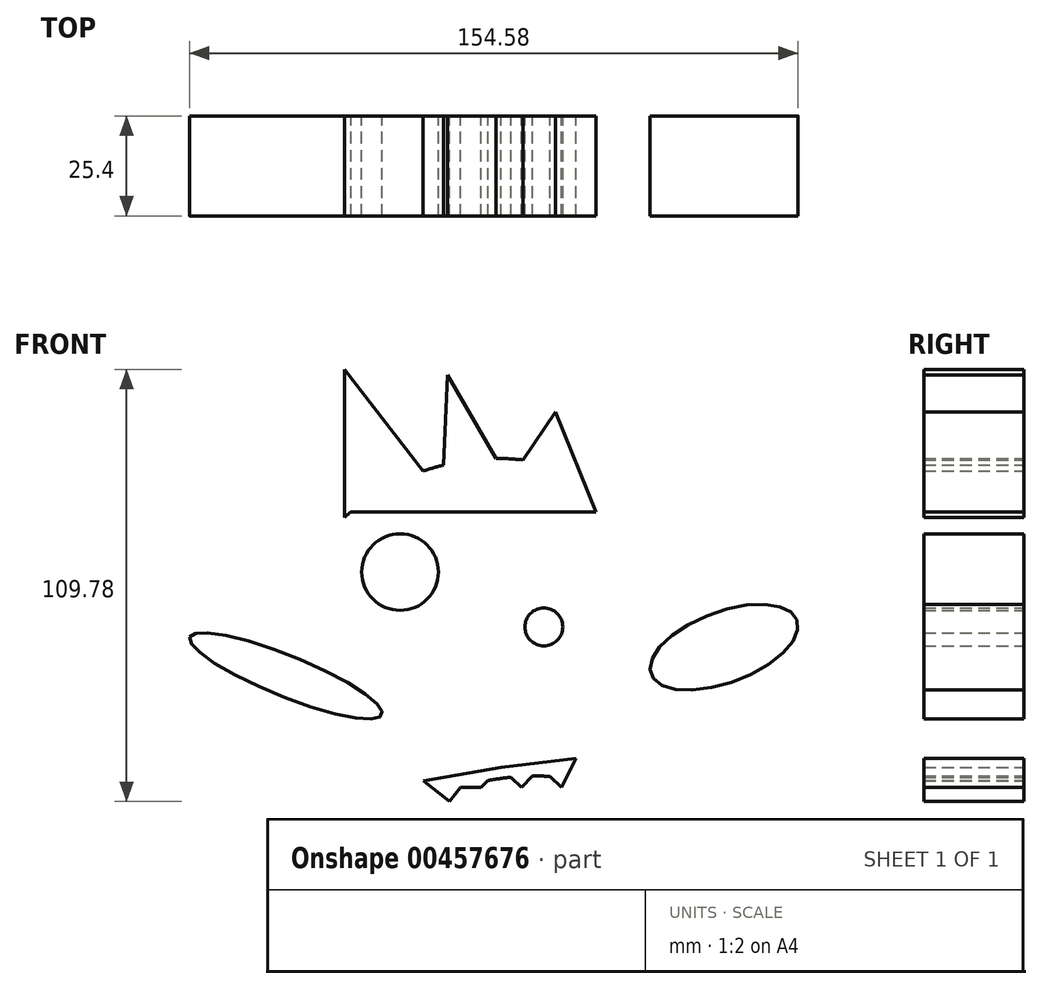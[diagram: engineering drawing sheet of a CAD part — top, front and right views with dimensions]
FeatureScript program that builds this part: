
annotation { "Feature Type Name" : "Feature", "Feature Type Description" : "" }
export const myFeature = defineFeature(function(context is Context, id is Id, definition is map)
    precondition{}
    {
        {
            var Q0;
            Q0=qCreatedBy(makeId("Front.planeOp"),FACE);
            var sketch = newSketch(context, id + "F0", { "sketchPlane" : qUnion([Q0])});
            skCircle(sketch, "E0", {"center": v(4.33, 0) * mm, "radius": 58.36 * mm});
            skCircle(sketch, "E1", {"center": v(-20.56, 29.51) * mm, "radius": 9.73 * mm});
            skCircle(sketch, "E2", {"center": v(17.31, 26.36) * mm, "radius": 10.85 * mm});
            skCircle(sketch, "E3", {"center": v(0, 0) * mm, "radius": 14.96 * mm});
            skArc(sketch, "E4", {"start": v(36.2, -26.36) * mm, "mid": v(6.21, -22.76) * mm, "end": v(-22.03, -33.44) * mm});
            skLineSegment(sketch, "E5", {"start": v(-22.03, -33.44) * mm, "end": v(36.2, -26.36) * mm});
            skLineSegment(sketch, "E6", {"start": v(-34.7, 43.39) * mm, "end": v(-34.7, 81) * mm});
            skLineSegment(sketch, "E7", {"start": v(-34.7, 81) * mm, "end": v(-9.93, 48.9) * mm});
            skLineSegment(sketch, "E8", {"start": v(-9.93, 48.9) * mm, "end": v(-8.51, 79.6) * mm});
            skLineSegment(sketch, "E9", {"start": v(-8.51, 79.6) * mm, "end": v(7.03, 52.73) * mm});
            skLineSegment(sketch, "E10", {"start": v(7.03, 52.73) * mm, "end": v(18.9, 70.15) * mm});
            skLineSegment(sketch, "E11", {"start": v(18.9, 70.15) * mm, "end": v(29.2, 44.82) * mm});
            skLineSegment(sketch, "E12", {"start": v(29.2, 44.82) * mm, "end": v(-33.05, 44.82) * mm});
            skEllipse(sketch, "E13", {"center": v(61.75, 10.44) * mm, "majorRadius": 19.75 * mm, "minorRadius": 9.04 * mm, "majorAxis": v(0.94, 0.35)});
            skEllipse(sketch, "E14", {"center": v(-49.58, 3.15) * mm, "majorRadius": 26.3 * mm, "minorRadius": 5.21 * mm, "majorAxis": v(-0.93, 0.37)});
            skLineSegment(sketch, "E15", {"start": v(-14.6, -23.54) * mm, "end": v(-8.05, -28.78) * mm});
            skLineSegment(sketch, "E16", {"start": v(-8.05, -28.78) * mm, "end": v(-5.23, -25.24) * mm});
            skLineSegment(sketch, "E17", {"start": v(-5.23, -25.24) * mm, "end": v(0, -25.24) * mm});
            skLineSegment(sketch, "E18", {"start": v(0, -25.24) * mm, "end": v(5.05, -20.13) * mm});
            skLineSegment(sketch, "E19", {"start": v(5.05, -20.13) * mm, "end": v(10.23, -25.24) * mm});
            skLineSegment(sketch, "E20", {"start": v(10.23, -25.24) * mm, "end": v(15.27, -20.13) * mm});
            skLineSegment(sketch, "E21", {"start": v(15.27, -20.13) * mm, "end": v(20.45, -25.24) * mm});
            skLineSegment(sketch, "E22", {"start": v(20.45, -25.24) * mm, "end": v(24.17, -17.77) * mm});
            skLineSegment(sketch, "E23", {"start": v(24.17, -17.77) * mm, "end": v(5.05, -20.13) * mm});
            skLineSegment(sketch, "E24", {"start": v(5.05, -20.13) * mm, "end": v(-14.6, -23.54) * mm});
            skCircle(sketch, "E25", {"center": v(15.96, 15.6) * mm, "radius": 4.8 * mm});
            skCircle(sketch, "E26", {"center": v(-20.56, 26.24) * mm, "radius": 3.46 * mm});
            skSolve(sketch);
        }
        {
            var Q0;
            {var subQ0=sQuery(id+"F0.wireOp",EDGE,"E13");var subQ1=sQuery(id+"F0.wireOp",EDGE,"E0");var subQ2=makeQuery(id+"F0.imprint","INTERSECT",VERTEX,{"disambiguationData":[OD(0.0)],"derivedFrom":[subQ1,subQ0]});Q0=makeQuery(id+"F0.imprint","IMPRINT",FACE,{"disambiguationData":[TD([[makeQuery(id+"F0.imprint","IMPRINT",EDGE,{"disambiguationData":[TD([[subQ2,1.0]])],"derivedFrom":subQ1}),-1.0]])]});}
            var Q1;
            {var subQ0=sQuery(id+"F0.wireOp",EDGE,"E11");var subQ1=sQuery(id+"F0.wireOp",EDGE,"E0");var subQ2=makeQuery(id+"F0.imprint","INTERSECT",VERTEX,{"derivedFrom":[subQ1,subQ0]});Q1=makeQuery(id+"F0.imprint","IMPRINT",FACE,{"disambiguationData":[TD([[makeQuery(id+"F0.imprint","IMPRINT",EDGE,{"disambiguationData":[TD([[subQ2,-1.0]])],"derivedFrom":subQ1}),-1.0]])]});}
            var Q2;
            {var subQ0=sQuery(id+"F0.wireOp",EDGE,"E10");var subQ1=sQuery(id+"F0.wireOp",EDGE,"E0");var subQ2=makeQuery(id+"F0.imprint","INTERSECT",VERTEX,{"derivedFrom":[subQ1,subQ0]});Q2=makeQuery(id+"F0.imprint","IMPRINT",FACE,{"disambiguationData":[TD([[makeQuery(id+"F0.imprint","IMPRINT",EDGE,{"disambiguationData":[TD([[subQ2,-1.0]])],"derivedFrom":subQ1}),1.0]])]});}
            var Q3;
            {var subQ0=sQuery(id+"F0.wireOp",EDGE,"E9");var subQ1=sQuery(id+"F0.wireOp",EDGE,"E0");var subQ2=makeQuery(id+"F0.imprint","INTERSECT",VERTEX,{"derivedFrom":[subQ1,subQ0]});Q3=makeQuery(id+"F0.imprint","IMPRINT",FACE,{"disambiguationData":[TD([[makeQuery(id+"F0.imprint","IMPRINT",EDGE,{"disambiguationData":[TD([[subQ2,-1.0]])],"derivedFrom":subQ1}),-1.0]])]});}
            var Q4;
            {var subQ0=sQuery(id+"F0.wireOp",EDGE,"E8");var subQ1=sQuery(id+"F0.wireOp",EDGE,"E0");var subQ2=makeQuery(id+"F0.imprint","INTERSECT",VERTEX,{"derivedFrom":[subQ1,subQ0]});Q4=makeQuery(id+"F0.imprint","IMPRINT",FACE,{"disambiguationData":[TD([[makeQuery(id+"F0.imprint","IMPRINT",EDGE,{"disambiguationData":[TD([[subQ2,-1.0]])],"derivedFrom":subQ1}),1.0]])]});}
            var Q5;
            {var subQ0=sQuery(id+"F0.wireOp",EDGE,"E14");var subQ1=sQuery(id+"F0.wireOp",EDGE,"E0");var subQ2=makeQuery(id+"F0.imprint","INTERSECT",VERTEX,{"disambiguationData":[OD(0.0)],"derivedFrom":[subQ1,subQ0]});Q5=makeQuery(id+"F0.imprint","IMPRINT",FACE,{"disambiguationData":[TD([[makeQuery(id+"F0.imprint","IMPRINT",EDGE,{"disambiguationData":[TD([[subQ2,-1.0]])],"derivedFrom":subQ1}),-1.0]])]});}
            var Q6;
            {var subQ0=sQuery(id+"F0.wireOp",EDGE,"E13");var subQ1=sQuery(id+"F0.wireOp",EDGE,"E0");var subQ2=makeQuery(id+"F0.imprint","INTERSECT",VERTEX,{"disambiguationData":[OD(0.0)],"derivedFrom":[subQ1,subQ0]});Q6=makeQuery(id+"F0.imprint","IMPRINT",FACE,{"disambiguationData":[TD([[makeQuery(id+"F0.imprint","IMPRINT",EDGE,{"disambiguationData":[TD([[subQ2,1.0]])],"derivedFrom":subQ1}),1.0]])]});}
            var Q7;
            {var subQ4=sQuery(id+"F0.wireOp",EDGE,"E6");Q7=makeQuery(id+"F0.imprint","IMPRINT",FACE,{"disambiguationData":[TD([[makeQuery(id+"F0.imprint","IMPRINT",EDGE,{"derivedFrom":subQ4}),-1.0]])]});}
            var Q8;
            {var subQ0=sQuery(id+"F0.wireOp",EDGE,"E14");var subQ1=sQuery(id+"F0.wireOp",EDGE,"E0");var subQ2=makeQuery(id+"F0.imprint","INTERSECT",VERTEX,{"disambiguationData":[OD(0.0)],"derivedFrom":[subQ1,subQ0]});Q8=makeQuery(id+"F0.imprint","IMPRINT",FACE,{"disambiguationData":[TD([[makeQuery(id+"F0.imprint","IMPRINT",EDGE,{"disambiguationData":[TD([[subQ2,-1.0]])],"derivedFrom":subQ1}),1.0]])]});}
            var Q9;
            {var subQ0=sQuery(id+"F0.wireOp",EDGE,"E12");Q9=makeQuery(id+"F0.imprint","IMPRINT",FACE,{"disambiguationData":[TD([[makeQuery(id+"F0.imprint","IMPRINT",EDGE,{"derivedFrom":subQ0}),-1.0]])]});}
            var Q10;
            {var subQ0=sQuery(id+"F0.wireOp",EDGE,"E20");var subQ1=sQuery(id+"F0.wireOp",EDGE,"E4");var subQ2=makeQuery(id+"F0.imprint","INTERSECT",VERTEX,{"derivedFrom":[subQ1,subQ0]});Q10=makeQuery(id+"F0.imprint","IMPRINT",FACE,{"disambiguationData":[TD([[makeQuery(id+"F0.imprint","IMPRINT",EDGE,{"disambiguationData":[TD([[subQ2,-1.0]])],"derivedFrom":subQ1}),1.0]])]});}
            var Q11;
            {var subQ0=sQuery(id+"F0.wireOp",EDGE,"E22");var subQ1=sQuery(id+"F0.wireOp",EDGE,"E4");var subQ2=makeQuery(id+"F0.imprint","INTERSECT",VERTEX,{"derivedFrom":[subQ1,subQ0]});Q11=makeQuery(id+"F0.imprint","IMPRINT",FACE,{"disambiguationData":[TD([[makeQuery(id+"F0.imprint","IMPRINT",EDGE,{"disambiguationData":[TD([[subQ2,-1.0]])],"derivedFrom":subQ1}),1.0]])]});}
            var Q12;
            {var subQ10=sQuery(id+"F0.wireOp",EDGE,"E23");Q12=makeQuery(id+"F0.imprint","IMPRINT",FACE,{"disambiguationData":[TD([[makeQuery(id+"F0.imprint","IMPRINT",EDGE,{"derivedFrom":subQ10}),1.0]])]});}
            var Q13;
            {var subQ0=sQuery(id+"F0.wireOp",EDGE,"E16");Q13=makeQuery(id+"F0.imprint","IMPRINT",FACE,{"disambiguationData":[TD([[makeQuery(id+"F0.imprint","IMPRINT",EDGE,{"derivedFrom":subQ0}),1.0]])]});}
            var Q14;
            {var subQ4=sQuery(id+"F0.wireOp",EDGE,"E24");Q14=makeQuery(id+"F0.imprint","IMPRINT",FACE,{"disambiguationData":[TD([[makeQuery(id+"F0.imprint","IMPRINT",EDGE,{"derivedFrom":subQ4}),1.0]])]});}
            var Q15;
            {var subQ0=sQuery(id+"F0.wireOp",EDGE,"E19");var subQ1=sQuery(id+"F0.wireOp",EDGE,"E4");var subQ2=makeQuery(id+"F0.imprint","INTERSECT",VERTEX,{"derivedFrom":[subQ1,subQ0]});Q15=makeQuery(id+"F0.imprint","IMPRINT",FACE,{"disambiguationData":[TD([[makeQuery(id+"F0.imprint","IMPRINT",EDGE,{"disambiguationData":[TD([[subQ2,-1.0]])],"derivedFrom":subQ1}),-1.0]])]});}
            var Q16;
            {var subQ0=sQuery(id+"F0.wireOp",EDGE,"E17");Q16=makeQuery(id+"F0.imprint","IMPRINT",FACE,{"disambiguationData":[TD([[makeQuery(id+"F0.imprint","IMPRINT",EDGE,{"derivedFrom":subQ0}),1.0]])]});}
            var Q17;
            {var subQ0=sQuery(id+"F0.wireOp",EDGE,"E21");var subQ1=sQuery(id+"F0.wireOp",EDGE,"E4");var subQ2=makeQuery(id+"F0.imprint","INTERSECT",VERTEX,{"derivedFrom":[subQ1,subQ0]});Q17=makeQuery(id+"F0.imprint","IMPRINT",FACE,{"disambiguationData":[TD([[makeQuery(id+"F0.imprint","IMPRINT",EDGE,{"disambiguationData":[TD([[subQ2,-1.0]])],"derivedFrom":subQ1}),-1.0]])]});}
            var Q18;
            {var subQ0=sQuery(id+"F0.wireOp",EDGE,"Bl3zAe94-TYqv-aWNH-iYuO-jx3CQXA83sbJ");var subQ1=sQuery(id+"F0.wireOp",EDGE,"E1");var subQ2=makeQuery(id+"F0.imprint","INTERSECT",VERTEX,{"disambiguationData":[OD(0.0)],"derivedFrom":[subQ1,subQ0]});Q18=makeQuery(id+"F0.imprint","IMPRINT",FACE,{"disambiguationData":[TD([[makeQuery(id+"F0.imprint","IMPRINT",EDGE,{"disambiguationData":[TD([[subQ2,-1.0]])],"derivedFrom":subQ1}),1.0]])]});}
            var Q19;
            Q19=makeQuery(id+"F0.imprint","IMPRINT",FACE,{"disambiguationData":[TD([[makeQuery(id+"F0.imprint","IMPRINT",EDGE,{"derivedFrom":sQuery(id+"F0.wireOp",EDGE,"E3")}),-1.0]])]});
            var Q20;
            {var subQ0=sQuery(id+"F0.wireOp",EDGE,"Bl3zAe94-TYqv-aWNH-iYuO-jx3CQXA83sbJ");var subQ1=sQuery(id+"F0.wireOp",EDGE,"E1");var subQ2=makeQuery(id+"F0.imprint","INTERSECT",VERTEX,{"disambiguationData":[OD(0.0)],"derivedFrom":[subQ1,subQ0]});Q20=makeQuery(id+"F0.imprint","IMPRINT",FACE,{"disambiguationData":[TD([[makeQuery(id+"F0.imprint","IMPRINT",EDGE,{"disambiguationData":[TD([[subQ2,-1.0]])],"derivedFrom":subQ1}),-1.0]])]});}
            var Q21;
            {var subQ0=sQuery(id+"F0.wireOp",EDGE,"E25");var subQ1=sQuery(id+"F0.wireOp",EDGE,"E2");var subQ2=makeQuery(id+"F0.imprint","INTERSECT",VERTEX,{"disambiguationData":[OD(0.0)],"derivedFrom":[subQ1,subQ0]});Q21=makeQuery(id+"F0.imprint","IMPRINT",FACE,{"disambiguationData":[TD([[makeQuery(id+"F0.imprint","IMPRINT",EDGE,{"disambiguationData":[TD([[subQ2,-1.0]])],"derivedFrom":subQ1}),1.0]])]});}
            var Q22;
            {var subQ0=sQuery(id+"F0.wireOp",EDGE,"E25");var subQ1=sQuery(id+"F0.wireOp",EDGE,"E2");var subQ2=makeQuery(id+"F0.imprint","INTERSECT",VERTEX,{"disambiguationData":[OD(0.0)],"derivedFrom":[subQ1,subQ0]});Q22=makeQuery(id+"F0.imprint","IMPRINT",FACE,{"disambiguationData":[TD([[makeQuery(id+"F0.imprint","IMPRINT",EDGE,{"disambiguationData":[TD([[subQ2,-1.0]])],"derivedFrom":subQ1}),-1.0]])]});}
            var Q23;
            Q23=makeQuery(id+"F0.imprint","IMPRINT",FACE,{"disambiguationData":[TD([[makeQuery(id+"F0.imprint","IMPRINT",EDGE,{"derivedFrom":sQuery(id+"F0.wireOp",EDGE,"E26")}),1.0]])]});
            extrude(context, id + "F1", {"entities" : qUnion([Q0, Q1, Q2, Q3, Q4, Q5, Q6, Q7, Q8, Q9, Q10, Q11, Q12, Q13, Q14, Q15, Q16, Q17, Q18, Q19, Q20, Q21, Q22, Q23]), "depth" : 25.4 * mm});
        }
        {
            var Q0;
            Q0=qCreatedBy(makeId("Top.planeOp"),FACE);
            cPlane(context, id + "F2", {"entities" : qUnion([Q0]), "cplaneType" : CPlaneType.OFFSET, "offset" : 76.2 * mm, "oppositeDirection" : true, "width" : 152.4 * mm, "height" : 152.4 * mm});
        }
        {
            var Q0;
            Q0=qCreatedBy(id+"F2.planeOp",FACE);
            var sketch = newSketch(context, id + "F3", { "sketchPlane" : qUnion([Q0])});
            skLineSegment(sketch, "E27.bottom", {"start": v(112.21, 55.9) * mm, "end": v(-106.58, 55.9) * mm});
            skLineSegment(sketch, "E27.top", {"start": v(112.21, -74.4) * mm, "end": v(-106.58, -74.4) * mm});
            skLineSegment(sketch, "E27.left", {"start": v(112.21, 55.9) * mm, "end": v(112.21, -74.4) * mm});
            skLineSegment(sketch, "E27.right", {"start": v(-106.58, 55.9) * mm, "end": v(-106.58, -74.4) * mm});
            skSolve(sketch);
        }
        {
            var Q0;
            Q0 = qSketchRegion(id + "F3", true);
            var Q1;
            Q1=sQuery(id+"F3.wireOp",EDGE,"E27.right");
            var Q2;
            Q2=sQuery(id+"F3.wireOp",EDGE,"E27.top");
            var Q3;
            Q3=sQuery(id+"F3.wireOp",EDGE,"E27.left");
            var Q4;
            Q4=sQuery(id+"F3.wireOp",EDGE,"E27.bottom");
            extrude(context, id + "F4", {"entities" : qUnion([Q0]), "bodyType" : ExtendedToolBodyType.SURFACE, "surfaceEntities" : qUnion([Q1, Q2, Q3, Q4]), "depth" : 152.4 * mm});
        }
    });
